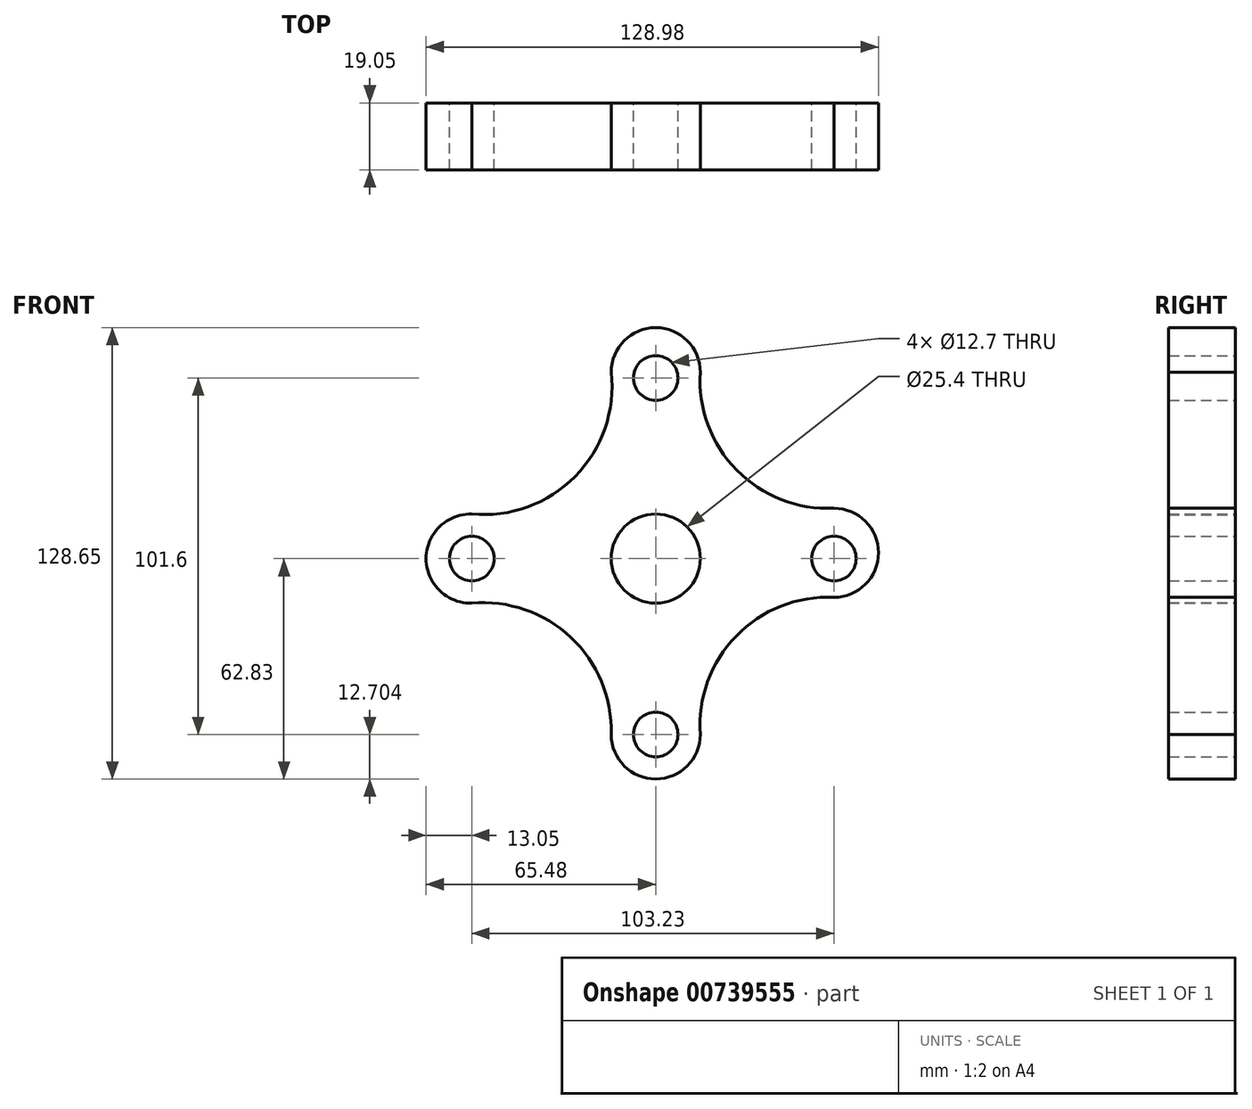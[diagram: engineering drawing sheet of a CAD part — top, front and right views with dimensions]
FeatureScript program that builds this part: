
annotation { "Feature Type Name" : "Feature", "Feature Type Description" : "" }
export const myFeature = defineFeature(function(context is Context, id is Id, definition is map)
    precondition{}
    {
        {
            var Q0;
            Q0=qCreatedBy(makeId("Front.planeOp"),FACE);
            var sketch = newSketch(context, id + "F0", { "sketchPlane" : qUnion([Q0])});
            skLineSegment(sketch, "E0", {"start": v(0, 45.12) * mm, "end": v(0, -50.13) * mm});
            skLineSegment(sketch, "E1", {"start": v(0, -50.13) * mm, "end": v(12.7, -50.13) * mm});
            skLineSegment(sketch, "E2", {"start": v(0, -50.13) * mm, "end": v(-12.7, -50.13) * mm});
            skCircle(sketch, "E3", {"center": v(0, 0) * mm, "radius": 12.7 * mm});
            skCircle(sketch, "E4", {"center": v(50.8, 0) * mm, "radius": 6.35 * mm});
            skCircle(sketch, "E5", {"center": v(0, 51.47) * mm, "radius": 6.35 * mm});
            skCircle(sketch, "E6", {"center": v(-52.43, 0) * mm, "radius": 6.35 * mm});
            skCircle(sketch, "E7", {"center": v(0, -50.13) * mm, "radius": 6.35 * mm});
            skPoint(sketch, "E8.orphan", {"position": v(-52.43, 25.38) * mm});
            skArc(sketch, "E9", {"start": v(-12.7, -50.13) * mm, "mid": v(0, -62.83) * mm, "end": v(12.7, -50.13) * mm});
            skArc(sketch, "E10", {"start": v(50.8, -11.05) * mm, "mid": v(63.5, 1.65) * mm, "end": v(50.8, 14.35) * mm});
            skArc(sketch, "E11", {"start": v(12.7, 53.12) * mm, "mid": v(0, 65.82) * mm, "end": v(-12.7, 53.12) * mm});
            skArc(sketch, "E12", {"start": v(-52.43, 12.7) * mm, "mid": v(-22.94, 23.45) * mm, "end": v(-12.7, 53.12) * mm});
            skArc(sketch, "E13", {"start": v(12.7, 53.12) * mm, "mid": v(23.1, 25.23) * mm, "end": v(50.8, 14.35) * mm});
            skArc(sketch, "E14", {"start": v(50.8, -11.05) * mm, "mid": v(22.98, -22.03) * mm, "end": v(12.7, -50.13) * mm});
            skArc(sketch, "E15", {"start": v(-12.7, -50.13) * mm, "mid": v(-24.16, -22.5) * mm, "end": v(-52.43, -12.7) * mm});
            skArc(sketch, "E16", {"start": v(-52.43, 12.7) * mm, "mid": v(-65.48, 0) * mm, "end": v(-52.43, -12.7) * mm});
            skSolve(sketch);
        }
        {
            var Q0;
            Q0 = qSketchRegion(id + "F0", true);
            extrude(context, id + "F1", {"entities" : qUnion([Q0]), "depth" : 19.05 * mm, "offsetDistance" : 25.4 * mm});
        }
        {
            var Q0;
            Q0 = qSketchRegion(id + "F0", true);
            extrude(context, id + "F2", {"entities" : qUnion([Q0]), "operationType" : NewBodyOperationType.ADD, "depth" : 19.05 * mm, "offsetDistance" : 25.4 * mm});
        }
    });
